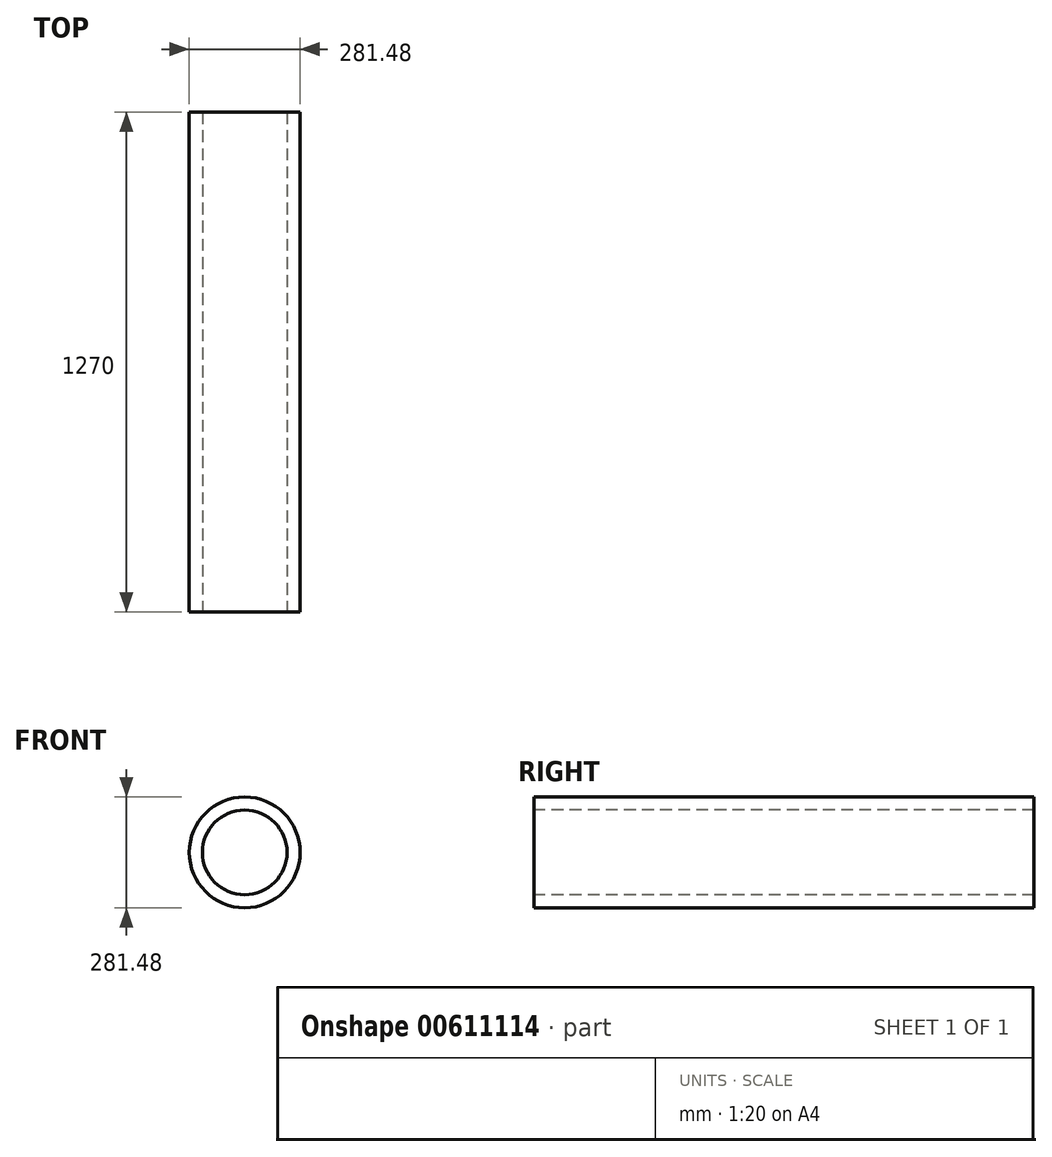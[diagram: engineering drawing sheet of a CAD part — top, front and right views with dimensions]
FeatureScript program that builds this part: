
annotation { "Feature Type Name" : "Feature", "Feature Type Description" : "" }
export const myFeature = defineFeature(function(context is Context, id is Id, definition is map)
    precondition{}
    {
        {
            var Q0;
            Q0=qCreatedBy(makeId("Front.planeOp"),FACE);
            var sketch = newSketch(context, id + "F0", { "sketchPlane" : qUnion([Q0])});
            skCircle(sketch, "E0", {"center": v(0, 0) * mm, "radius": 140.74 * mm});
            skCircle(sketch, "E1", {"center": v(0, 0) * mm, "radius": 107.5 * mm});
            skSolve(sketch);
        }
        {
            var Q0;
            Q0=sQuery(id+"F0.wireOp",EDGE,"E1");
            var Q1;
            Q1=sQuery(id+"F0.wireOp",EDGE,"E0");
            extrude(context, id + "F1", {"bodyType" : ToolBodyType.SURFACE, "surfaceEntities" : qUnion([Q0, Q1]), "depth" : 1270 * mm, "offsetDistance" : 25.4 * mm});
        }
    });
